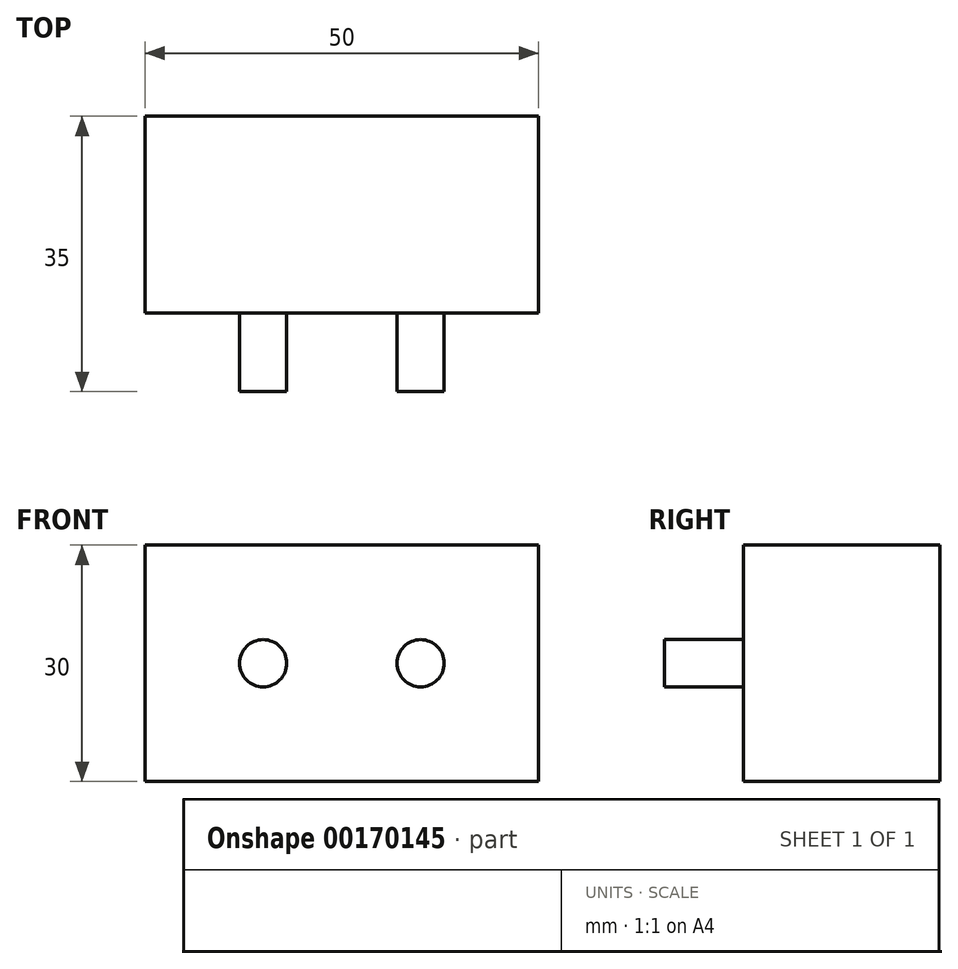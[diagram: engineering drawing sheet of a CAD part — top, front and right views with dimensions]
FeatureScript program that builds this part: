
annotation { "Feature Type Name" : "Feature", "Feature Type Description" : "" }
export const myFeature = defineFeature(function(context is Context, id is Id, definition is map)
    precondition{}
    {
        {
            var Q0;
            Q0=qCreatedBy(makeId("Front.planeOp"),FACE);
            var sketch = newSketch(context, id + "F0", { "sketchPlane" : qUnion([Q0])});
            skLineSegment(sketch, "E0.bottom", {"start": v(25, 15) * mm, "end": v(-25, 15) * mm});
            skLineSegment(sketch, "E0.top", {"start": v(25, -15) * mm, "end": v(-25, -15) * mm});
            skLineSegment(sketch, "E0.left", {"start": v(25, 15) * mm, "end": v(25, -15) * mm});
            skLineSegment(sketch, "E0.right", {"start": v(-25, 15) * mm, "end": v(-25, -15) * mm});
            skPoint(sketch, "E0.middle", {"position": v(0, 0) * mm});
            skSolve(sketch);
        }
        {
            var Q0;
            Q0=makeQuery(id+"F0.imprint","IMPRINT",FACE,{"disambiguationData":[TD([[makeQuery(id+"F0.imprint","IMPRINT",EDGE,{"derivedFrom":sQuery(id+"F0.wireOp",EDGE,"E0.bottom")}),1.0]])]});
            extrude(context, id + "F1", {"entities" : qUnion([Q0]), "depth" : 25 * mm});
        }
        {
            var Q0;
            Q0=makeQuery(id+"F1.opExtrude","CAP_FACE",FACE,{"disambiguationData":[OSD([sQuery(id+"F0.wireOp",EDGE,"E0.bottom"),sQuery(id+"F0.wireOp",EDGE,"E0.top"),sQuery(id+"F0.wireOp",EDGE,"E0.left"),sQuery(id+"F0.wireOp",EDGE,"E0.right")])],"isStart":false});
            var sketch = newSketch(context, id + "F2", { "sketchPlane" : qUnion([Q0])});
            skCircle(sketch, "E1", {"center": v(-10, 0) * mm, "radius": 3 * mm});
            skCircle(sketch, "E2", {"center": v(10, 0) * mm, "radius": 3 * mm});
            skSolve(sketch);
        }
        {
            var Q0;
            Q0=makeQuery(id+"F2.imprint","IMPRINT",FACE,{"disambiguationData":[TD([[makeQuery(id+"F2.imprint","IMPRINT",EDGE,{"derivedFrom":sQuery(id+"F2.wireOp",EDGE,"E1")}),1.0]])]});
            var Q1;
            Q1=makeQuery(id+"F2.imprint","IMPRINT",FACE,{"disambiguationData":[TD([[makeQuery(id+"F2.imprint","IMPRINT",EDGE,{"derivedFrom":sQuery(id+"F2.wireOp",EDGE,"E2")}),1.0]])]});
            extrude(context, id + "F3", {"entities" : qUnion([Q0, Q1]), "operationType" : NewBodyOperationType.ADD, "depth" : 10 * mm});
        }
    });
